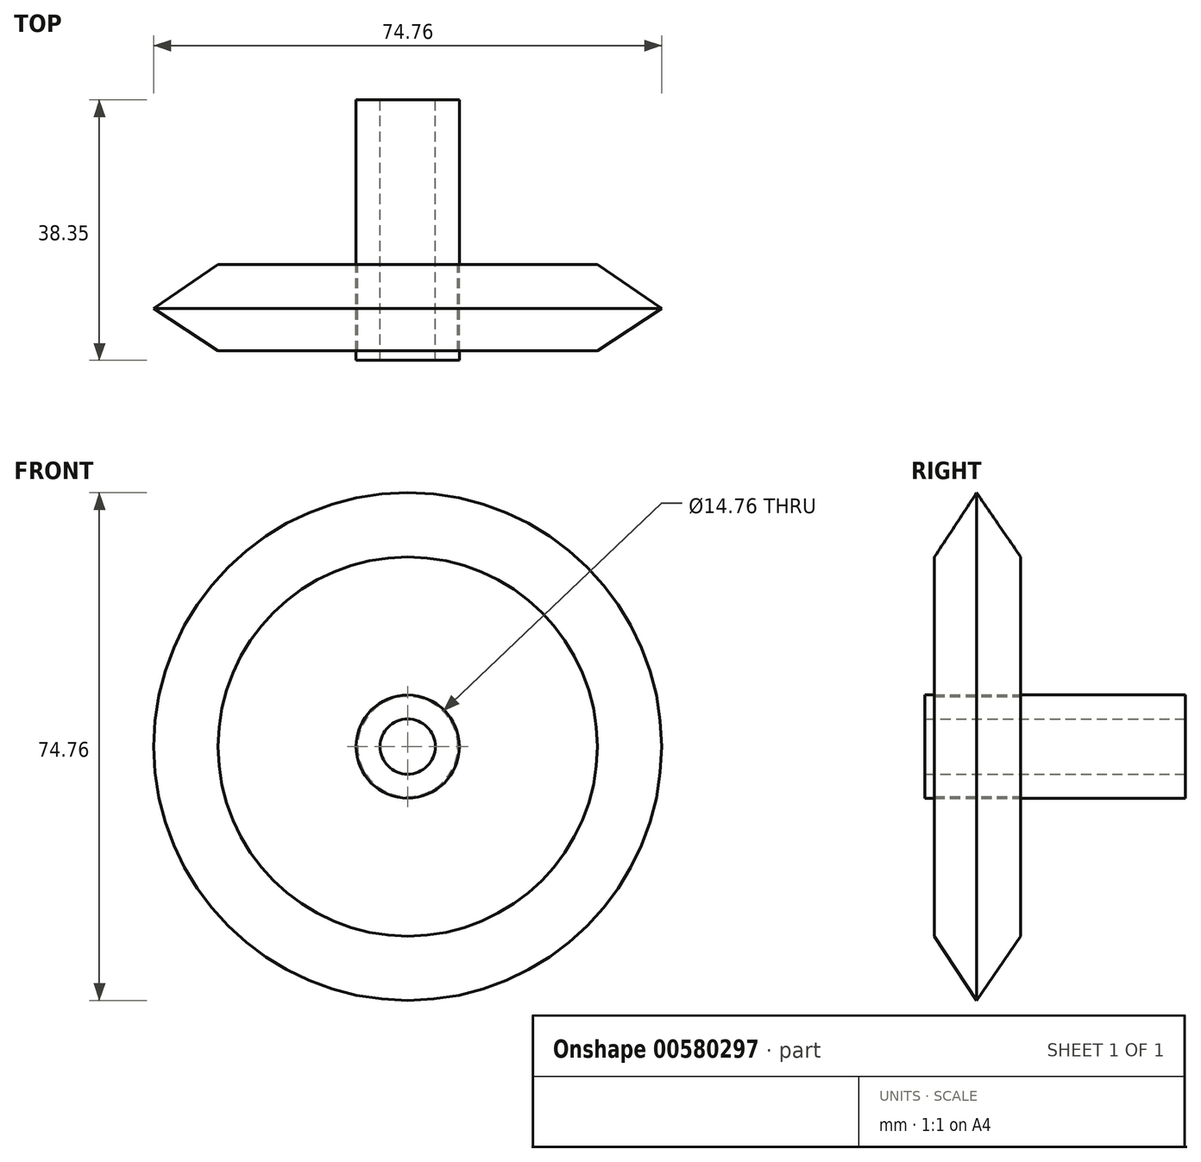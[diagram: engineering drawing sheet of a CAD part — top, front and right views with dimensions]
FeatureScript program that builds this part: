
annotation { "Feature Type Name" : "Feature", "Feature Type Description" : "" }
export const myFeature = defineFeature(function(context is Context, id is Id, definition is map)
    precondition{}
    {
        {
            var Q0;
            Q0=qCreatedBy(makeId("Right.planeOp"),FACE);
            var sketch = newSketch(context, id + "F0", { "sketchPlane" : qUnion([Q0])});
            skLineSegment(sketch, "E0.bottom", {"start": v(-24.25, 7.38) * mm, "end": v(-36.95, 7.38) * mm});
            skLineSegment(sketch, "E0.top", {"start": v(-24.25, 27.92) * mm, "end": v(-36.95, 27.92) * mm});
            skLineSegment(sketch, "E0.left", {"start": v(-24.25, 7.38) * mm, "end": v(-24.25, 27.92) * mm});
            skLineSegment(sketch, "E0.right", {"start": v(-36.95, 7.38) * mm, "end": v(-36.95, 27.92) * mm});
            skLineSegment(sketch, "E1", {"start": v(-36.95, 27.92) * mm, "end": v(-30.74, 37.38) * mm});
            skLineSegment(sketch, "E2", {"start": v(-30.74, 37.38) * mm, "end": v(-24.25, 27.92) * mm});
            skLineSegment(sketch, "E3", {"start": v(0, 0) * mm, "end": v(-48.57, 0) * mm});
            skSolve(sketch);
        }
        {
            var Q0;
            Q0=makeQuery(id+"F0.imprint","IMPRINT",FACE,{"disambiguationData":[TD([[makeQuery(id+"F0.imprint","IMPRINT",EDGE,{"derivedFrom":sQuery(id+"F0.wireOp",EDGE,"E0.top")}),-1.0]])]});
            var Q1;
            Q1=makeQuery(id+"F0.imprint","IMPRINT",FACE,{"disambiguationData":[TD([[makeQuery(id+"F0.imprint","IMPRINT",EDGE,{"derivedFrom":sQuery(id+"F0.wireOp",EDGE,"E0.bottom")}),-1.0]])]});
            var Q2;
            Q2=sQuery(id+"F0.wireOp",EDGE,"E3");
            revolve(context, id + "F1", {"entities" : qUnion([Q0, Q1]), "axis" : qUnion([Q2]), "revolveType" : RevolveType.FULL});
        }
        {
            var Q0;
            Q0=qCreatedBy(makeId("Front.planeOp"),FACE);
            var sketch = newSketch(context, id + "F2", { "sketchPlane" : qUnion([Q0])});
            skCircle(sketch, "E4", {"center": v(0, 0) * mm, "radius": 7.6 * mm});
            skSolve(sketch);
        }
        {
            var Q0;
            Q0 = qSketchRegion(id + "F2", true);
            extrude(context, id + "F3", {"entities" : qUnion([Q0]), "depth" : 38.35 * mm, "offsetDistance" : 25.4 * mm});
        }
        {
            var Q0;
            Q0=qCreatedBy(makeId("Front.planeOp"),FACE);
            var sketch = newSketch(context, id + "F4", { "sketchPlane" : qUnion([Q0])});
            skCircle(sketch, "E5", {"center": v(0, 0) * mm, "radius": 4.03 * mm});
            skSolve(sketch);
        }
        {
            var Q0;
            Q0=sQuery(id+"F4.wireOp",VERTEX,"E5.center");
            var Q1;
            Q1=makeQuery(id+"F3.opExtrude","SWEPT_BODY",BODY,{"disambiguationData":[OSD([sQuery(id+"F2.wireOp",EDGE,"E4")])]});
            hole(context, id + "F5", {"style" : HoleStyle.SIMPLE, "endStyle" : HoleEndStyle.THROUGH, "oppositeDirection" : true, "holeDiameter" : 8.13 * mm, "majorDiameter" : 6.35 * mm, "isTappedThrough" : true, "tappedDepth" : 12.7 * mm, "tapClearance" : 3, "locations" : qUnion([Q0]), "scope" : qUnion([Q1])});
        }
    });
